FCSTD DOCUMENT  (FreeCAD 0.19R)
Label: Printer_assembly
License: All rights reserved
LicenseURL: http://en.wikipedia.org/wiki/All_rights_reserved
objects: App::Link×12, App::DocumentObjectGroup×4, Part::FeaturePython×2, App::AnnotationLabel×2, PartDesign::CoordinateSystem×1, App::FeaturePython×1, App::Part×1
note: 3 computed .brp shape members not serialized (recipe doc carries the construction recipe); baked Part::Feature solids carry a one-line shape summary decoded from their .brp
EXTERNAL_REF file=bed_aluminum.FCStd obj=Local_CS
EXTERNAL_REF file=bed_aluminum.FCStd obj=Body
EXTERNAL_REF file=extruder_head_gear.FCStd obj=Local_CS001
EXTERNAL_REF file=extruder_head_gear.FCStd obj=Body
EXTERNAL_REF file=angle_machined_2in_25.FCStd obj=Local_CS004
EXTERNAL_REF file=extruder_head_gear.FCStd obj=Local_CS
EXTERNAL_REF file=angle_machined_2in_25.FCStd obj=Body
EXTERNAL_REF file=angle_machined_2in_25.FCStd obj=Local_CS
EXTERNAL_REF file=motor stepper extruder.FCStd obj=Local_CS001
EXTERNAL_REF file=motor stepper extruder.FCStd obj=Body
EXTERNAL_REF file=angle_machined_2in_25.FCStd obj=Local_CS001
EXTERNAL_REF file=bearing_linear_8mm.FCStd obj=Local_CS
EXTERNAL_REF file=bearing_linear_8mm.FCStd obj=Body
EXTERNAL_REF file=angle_machined_2in_25.FCStd obj=Local_CS002
EXTERNAL_REF file=bearing_linear_8mm.FCStd obj=Local_CS001
EXTERNAL_REF file=screw_shc_M3x12.FCStd obj=Local_CS
EXTERNAL_REF file=screw_shc_M3x12.FCStd obj=Body
EXTERNAL_REF file=angle_machined_2in_25.FCStd obj=Local_CS005
EXTERNAL_REF file=washer_M5.FCStd obj=Local_CS
EXTERNAL_REF file=washer_M5.FCStd obj=Body
EXTERNAL_REF file=screw_shc_M3x16.FCStd obj=Local_CS
EXTERNAL_REF file=screw_shc_M3x16.FCStd obj=Body
EXTERNAL_REF file=Hex_Nut_M3.FCstd obj=Local_CS
EXTERNAL_REF file=washer_M5.FCStd obj=Local_CS001
EXTERNAL_REF file=Hex_Nut_M3.FCstd obj=Body
EXTERNAL_REF file=angle_machined_2in_25.FCStd obj=Local_CS006
EXTERNAL_REF file=nut_lead_screw_tr8x4.FCStd obj=Local_CS001
EXTERNAL_REF file=nut_lead_screw_tr8x4.FCStd obj=Body
EXTERNAL_REF file=drive_side_x-axis.FCStd obj=LCS_Origin
EXTERNAL_REF file=drive_side_x-axis.FCStd obj=Assembly

FEATURE [App::DocumentObjectGroup] Parts
FEATURE [PartDesign::CoordinateSystem] LCS_Origin
  AttacherType = Attacher::AttachEngine3D
  MapMode = 2
  Support = -> [X_Axis]
FEATURE [App::FeaturePython] Variables  # WARN: FeaturePython — macro-defined, semantics opaque (R4)
  Type = App::PropertyContainer
FEATURE [App::DocumentObjectGroup] Constraints
FEATURE [App::DocumentObjectGroup] Configurations
FEATURE [App::Link] bed
  AttachedBy = #Local_CS
  AttachedTo = Parent Assembly#LCS_Origin
  LinkPlacement = pos=(0,0,-6.35) rot=(0,0,1;0rad)
  LinkedObject = -> <external bed_aluminum.FCStd>#Body
  Placement = pos=(0,0,-6.35) rot=(0,0,1;0rad)
  SolverId = Placement::ExpressionEngine
  expr: Placement = LCS_Origin.Placement * AttachmentOffset * bed_aluminum#Local_CS.Placement ^ -1
FEATURE [App::Link] Body  label="Extruder"
  AttachedBy = #Local_CS001
  AttachedTo = bed#Local_CS
  AttachmentOffset = pos=(0,0,310) rot=(0,0,1;0rad)
  LinkPlacement = pos=(-15,-0.9652,380) rot=(0,0,1;0rad)
  LinkedObject = -> <external extruder_head_gear.FCStd>#Body
  Placement = pos=(-15,-0.9652,380) rot=(0,0,1;0rad)
  SolverId = Placement::ExpressionEngine
  expr: Placement = bed.Placement * bed_aluminum#Local_CS.Placement * AttachmentOffset * extruder_head_gear#Local_CS001.Placement ^ -1
FEATURE [App::Link] Bracket_extruder
  AttachedBy = #Local_CS004
  AttachedTo = Body#Local_CS
  AttachmentOffset = pos=(0,0,0) rot=(0,1,0;3.14159rad)
  LinkPlacement = pos=(-43,13.716,380) rot=(-1,0,0;3.14159rad)
  LinkedObject = -> <external angle_machined_2in_25.FCStd>#Body
  Placement = pos=(-43,13.716,380) rot=(-1,0,0;3.14159rad)
  SolverId = Placement::ExpressionEngine
  expr: Placement = Body.Placement * extruder_head_gear#Local_CS.Placement * AttachmentOffset * angle_machined_2in_25#Local_CS004.Placement ^ -1
FEATURE [App::Link] Body001  label="Motor_extruder"
  AttachedBy = #Local_CS001
  AttachedTo = Bracket_extruder#Local_CS
  AttachmentOffset = pos=(0,0,0) rot=(0,0,1;1.5708rad)
  LinkPlacement = pos=(-15,42.4785,380) rot=(-0.57735,-0.57735,0.57735;4.18879rad)
  LinkedObject = -> <external motor stepper extruder.FCStd>#Body
  Placement = pos=(-15,42.4785,380) rot=(-0.57735,-0.57735,0.57735;4.18879rad)
  SolverId = Placement::ExpressionEngine
  expr: Placement = Bracket_extruder.Placement * angle_machined_2in_25#Local_CS.Placement * AttachmentOffset * motor_stepper_extruder#Local_CS001.Placement ^ -1
FEATURE [App::Link] bearing_linear_8mm
  AttachedBy = #Local_CS
  AttachedTo = Bracket_extruder#Local_CS001
  AttachmentOffset = pos=(0,0,0) rot=(0,1,0;3.14159rad)
  LinkPlacement = pos=(-48,27.716,420) rot=(0.57735,-0.57735,0.57735;4.18879rad)
  LinkedObject = -> <external bearing_linear_8mm.FCStd>#Body
  Placement = pos=(-48,27.716,420) rot=(0.57735,-0.57735,0.57735;4.18879rad)
  SolverId = Placement::ExpressionEngine
  expr: Placement = Bracket_extruder.Placement * angle_machined_2in_25#Local_CS001.Placement * AttachmentOffset * bearing_linear_8mm#Local_CS.Placement ^ -1
FEATURE [App::Link] Body002  label="bearing_linear_8mm_2"
  AttachedBy = #Local_CS
  AttachedTo = Bracket_extruder#Local_CS002
  AttachmentOffset = pos=(0,0,0) rot=(0,1,0;3.14159rad)
  LinkPlacement = pos=(-48,27.716,340) rot=(0.57735,-0.57735,0.57735;4.18879rad)
  LinkedObject = -> <external bearing_linear_8mm.FCStd>#Body
  Placement = pos=(-48,27.716,340) rot=(0.57735,-0.57735,0.57735;4.18879rad)
  SolverId = Placement::ExpressionEngine
  expr: Placement = Bracket_extruder.Placement * angle_machined_2in_25#Local_CS002.Placement * AttachmentOffset * bearing_linear_8mm#Local_CS.Placement ^ -1
FEATURE [App::Link] screw_shc_M3x12
  AttachedBy = #Local_CS
  AttachedTo = bearing_linear_8mm#Local_CS001
  LinkPlacement = pos=(-32.9,27.716,432) rot=(0.57735,0.57735,0.57735;2.0944rad)
  LinkedObject = -> <external screw_shc_M3x12.FCStd>#Body
  Placement = pos=(-32.9,27.716,432) rot=(0.57735,0.57735,0.57735;2.0944rad)
  SolverId = Placement::ExpressionEngine
  expr: Placement = bearing_linear_8mm.Placement * bearing_linear_8mm#Local_CS001.Placement * AttachmentOffset * screw_shc_M3x12#Local_CS.Placement ^ -1
FEATURE [App::Link] washer_M5
  AttachedBy = #Local_CS
  AttachedTo = Bracket_extruder#Local_CS005
  LinkPlacement = pos=(-36.4,27.716,432) rot=(0,0,-1;1.5708rad)
  LinkedObject = -> <external washer_M5.FCStd>#Body
  Placement = pos=(-36.4,27.716,432) rot=(0,0,-1;1.5708rad)
  SolverId = Placement::ExpressionEngine
  expr: Placement = Bracket_extruder.Placement * angle_machined_2in_25#Local_CS005.Placement * AttachmentOffset * washer_M5#Local_CS.Placement ^ -1
FEATURE [App::Link] screw_shc_m3x16
  AttachedBy = #Local_CS
  AttachedTo = bearing_linear_8mm#Local_CS001
  LinkPlacement = pos=(-28.9,27.716,432) rot=(0.57735,0.57735,0.57735;2.0944rad)
  LinkedObject = -> <external screw_shc_M3x16.FCStd>#Body
  Placement = pos=(-28.9,27.716,432) rot=(0.57735,0.57735,0.57735;2.0944rad)
  SolverId = Placement::ExpressionEngine
  expr: Placement = bearing_linear_8mm.Placement * bearing_linear_8mm#Local_CS001.Placement * AttachmentOffset * screw_shc_M3x16#Local_CS.Placement ^ -1
FEATURE [App::Link] Body003  label="M3_nut"
  AttachedBy = #Local_CS
  AttachedTo = washer_M5#Local_CS001
  AttachmentOffset = pos=(0,0,0) rot=(0,1,0;3.14159rad)
  LinkPlacement = pos=(-34.95,27.716,432) rot=(0.250563,-0.935113,-0.250563;1.63783rad)
  LinkedObject = -> <external Hex_Nut_M3.FCstd>#Body
  Placement = pos=(-34.95,27.716,432) rot=(0.250563,-0.935113,-0.250563;1.63783rad)
  SolverId = Placement::ExpressionEngine
  expr: Placement = washer_M5.Placement * washer_M5#Local_CS001.Placement * AttachmentOffset * Hex_Nut_M3#Local_CS.Placement ^ -1
FEATURE [App::Link] nut_lead_screw_y
  AttachedBy = #Local_CS001
  AttachedTo = Bracket_extruder#Local_CS006
  LinkPlacement = pos=(-47,52.716,380) rot=(-0.678598,0.281085,0.678598;3.68962rad)
  LinkedObject = -> <external nut_lead_screw_tr8x4.FCStd>#Body
  Placement = pos=(-47,52.716,380) rot=(-0.678598,0.281085,0.678598;3.68962rad)
  SolverId = Placement::ExpressionEngine
  expr: Placement = Bracket_extruder.Placement * angle_machined_2in_25#Local_CS006.Placement * AttachmentOffset * nut_lead_screw_tr8x4#Local_CS001.Placement ^ -1
FEATURE [App::Link] drive_side_x_axis
  AttachedBy = #LCS_Origin
  AttachedTo = nut_lead_screw_y#Local_CS001
  AttachmentOffset = pos=(0,0,249.35) rot=(0,1,0;3.14159rad)
  LinkPlacement = pos=(206.35,52.716,380) rot=(0,1,0;4.71239rad)
  LinkedObject = -> <external drive_side_x-axis.FCStd>#Assembly
  Placement = pos=(206.35,52.716,380) rot=(0,1,0;4.71239rad)
  SolverId = Placement::ExpressionEngine
  expr: Placement = nut_lead_screw_y.Placement * nut_lead_screw_tr8x4#Local_CS001.Placement * AttachmentOffset * drive_side_x_axis#LCS_Origin.Placement ^ -1
FEATURE [App::Part] Assembly
  AssemblyType = Part::Link
  Group = -> [LCS_Origin,Variables,Constraints,Configurations,bed,Body,Bracket_extruder,Body001,bearing_linear_8mm,Body002,screw_shc_M3x12,washer_M5,screw_shc_m3x16,Body003,nut_lead_screw_y,drive_side_x_axis]
  Origin = -> Origin
  Type = Assembly
FEATURE [Part::FeaturePython] DistPoints  # WARN: FeaturePython — macro-defined, semantics opaque (R4)
FEATURE [App::AnnotationLabel] MeasureLbl
  BasePosition = (-206.5,13.716,320)
  LabelText = D = 13.0000 mm
  TextPosition = (0,0,0)
FEATURE [Part::FeaturePython] DistPoints001  # WARN: FeaturePython — macro-defined, semantics opaque (R4)
FEATURE [App::AnnotationLabel] MeasureLbl001
  BasePosition = (225.4,19.916,411)
  LabelText = D  = 81.1073 mm | ΔX = -50.799 | ΔY = 12.400 | ΔZ = 62.000
  TextPosition = (0,0,0)
FEATURE [App::DocumentObjectGroup] Measures
  Group = -> [DistPoints,MeasureLbl,DistPoints001,MeasureLbl001]

RESOLVED EXTERNAL PARTS (link-assembly join: the EXTERNAL_REF files above that resolve inside this repo's crawl, each included once):
---- part Hex_Nut_M3.FCstd = doc fcstd_daaefb471c37 ----
FCSTD DOCUMENT  (FreeCAD 0.19R)
Label: Hex_Nut_M3
License: All rights reserved
LicenseURL: http://en.wikipedia.org/wiki/All_rights_reserved
objects: PartDesign::CoordinateSystem×2, Part::Feature×1, PartDesign::FeatureBase×1, PartDesign::Body×1
note: 5 computed .brp shape members not serialized (recipe doc carries the construction recipe); baked Part::Feature solids carry a one-line shape summary decoded from their .brp

FEATURE [Part::Feature] _1828A211_18_8_Stainless_Steel_Hex_Nut
  shape: bbox 6.351 x 6.351 x 2.771 mm, 48 faces, 0 solids (baked)
FEATURE [PartDesign::FeatureBase] BaseFeature
  BaseFeature = -> _1828A211_18_8_Stainless_Steel_Hex_Nut
FEATURE [PartDesign::CoordinateSystem] Local_CS
  AttacherType = Attacher::AttachEngine3D
  MapMode = 11
  Placement = pos=(-4e-16,4e-16,1.2) rot=(-0.258819,0.965926,0;3.14159rad)
  Support = -> [BaseFeature]
FEATURE [PartDesign::CoordinateSystem] Local_CS001
  AttacherType = Attacher::AttachEngine3D
  AttachmentOffset = pos=(0,0,0) rot=(0,0,1;1.5708rad)
  MapMode = 11
  Placement = pos=(7e-16,-4e-16,-1.2) rot=(0,0,1;2.0944rad)
  Support = -> [BaseFeature]
FEATURE [PartDesign::Body] Body
  BaseFeature = -> _1828A211_18_8_Stainless_Steel_Hex_Nut
  Group = -> [BaseFeature,Local_CS,Local_CS001]
  Origin = -> Origin
  Tip = -> BaseFeature
---- part angle_machined_2in_25.FCStd = doc fcstd_c500b0d28d3c ----
FCSTD DOCUMENT  (FreeCAD 0.19R)
Label: angle_machined_2in_25
License: All rights reserved
LicenseURL: http://en.wikipedia.org/wiki/All_rights_reserved
objects: Sketcher::SketchObject×7, PartDesign::CoordinateSystem×7, PartDesign::Pocket×6, PartDesign::Pad×2, PartDesign::Mirrored×2, PartDesign::Fillet×1, PartDesign::LinearPattern×1, PartDesign::Body×1
note: 36 computed .brp shape members not serialized (recipe doc carries the construction recipe); baked Part::Feature solids carry a one-line shape summary decoded from their .brp

FEATURE [Sketcher::SketchObject] Sketch
  FullyConstrained = true
  MapMode = 5
  Support = -> [XY_Plane]
  sketch-geometry (6):
    g0: LineSegment StartX=0 StartY=0 StartZ=0 EndX=50.8 EndY=0 EndZ=0
    g1: LineSegment StartX=50.8 StartY=0 StartZ=0 EndX=50.8 EndY=-6.35 EndZ=0
    g2: LineSegment StartX=50.8 StartY=-6.35 StartZ=0 EndX=6.35 EndY=-6.35 EndZ=0
    g3: LineSegment StartX=6.35 StartY=-6.35 StartZ=0 EndX=6.35 EndY=-50.8 EndZ=0
    g4: LineSegment StartX=6.35 StartY=-50.8 StartZ=0 EndX=0 EndY=-50.8 EndZ=0
    g5: LineSegment StartX=0 StartY=-50.8 StartZ=0 EndX=0 EndY=0 EndZ=0
  constraints (17):
    c: Coincident(g-1,g0)
    c: PointOnObject(g0,g-1)
    c: Coincident(g0,g1)
    c: Vertical(g1)
    c: Coincident(g1,g2)
    c: Horizontal(g2)
    c: Coincident(g2,g3)
    c: Vertical(g3)
    c: Coincident(g3,g4)
    c: PointOnObject(g4,g-2)
    c: Horizontal(g4)
    c: Coincident(g4,g5)
    c: Coincident(g5,g0)
    c: Equal(g1,g4)
    c: DistanceY(g1,g1) = 6.35
    c: DistanceX(g0,g0) = 50.8
    c: Equal(g0,g5)
FEATURE [PartDesign::Pad] Pad
  Direction = (1,1,1)
  Length = 56
  Length2 = 100
  Profile = -> Sketch
  Refine = true
  Reversed = true
  Type = 0
FEATURE [Sketcher::SketchObject] Sketch001
  FullyConstrained = true
  MapMode = 5
  Placement = pos=(0,0,0) rot=(0.57735,0.57735,0.57735;2.0944rad)
  Support = -> [YZ_Plane]
  sketch-geometry (3):
    g0: Circle CenterX=-14 CenterY=-40 CenterZ=0 NormalX=0 NormalY=0 NormalZ=1 AngleXU=0 Radius=7.9375
    g1: Circle CenterX=-14 CenterY=-28 CenterZ=0 NormalX=0 NormalY=0 NormalZ=1 AngleXU=0 Radius=2
    g2: Circle CenterX=-14 CenterY=-52 CenterZ=0 NormalX=0 NormalY=0 NormalZ=1 AngleXU=0 Radius=2
  constraints (8):
    c: Diameter(g0) = 15.875
    c: Diameter(g1) = 4
    c: Equal(g1,g2)
    c: Symmetric(g1,g2,g0)
    c: Vertical(g1,g0)
    c: Distance(g1,g2) = 24
    c: DistanceX(g0,g-1) = 14
    c: DistanceY(g0,g-1) = 40
FEATURE [Sketcher::SketchObject] Sketch002
  FullyConstrained = true
  MapMode = 5
  Placement = pos=(0,0,0) rot=(0.57735,0.57735,0.57735;2.0944rad)
  Support = -> [YZ_Plane]
  sketch-geometry (8):
    g0: Circle CenterX=-39 CenterY=0 CenterZ=0 NormalX=0 NormalY=0 NormalZ=1 AngleXU=0 Radius=5.35781
    g1: Circle CenterX=-39 CenterY=0 CenterZ=0 NormalX=0 NormalY=0 NormalZ=1 AngleXU=0 Radius=8
    g2: Circle CenterX=-44.6569 CenterY=5.65685 CenterZ=0 NormalX=0 NormalY=0 NormalZ=1 AngleXU=0 Radius=1.5875
    g3: Circle CenterX=-33.3431 CenterY=5.65685 CenterZ=0 NormalX=0 NormalY=0 NormalZ=1 AngleXU=0 Radius=1.5875
    g4: Circle CenterX=-33.3431 CenterY=-5.65685 CenterZ=0 NormalX=0 NormalY=0 NormalZ=1 AngleXU=0 Radius=1.5875
    g5: Circle CenterX=-44.6569 CenterY=-5.65685 CenterZ=0 NormalX=0 NormalY=0 NormalZ=1 AngleXU=0 Radius=1.5875
    g6: LineSegment StartX=-44.6569 StartY=5.65685 StartZ=0 EndX=-33.3431 EndY=5.65685 EndZ=0
    g7: LineSegment StartX=-33.3431 StartY=5.65685 StartZ=0 EndX=-33.3431 EndY=-5.65685 EndZ=0
  constraints (19):
    c: Diameter(g0) = 10.7156
    c: Horizontal(g0,g-1)
    c: Coincident(g1,g0)
    c: Diameter(g1) = 16
    c: PointOnObject(g2,g1)
    c: PointOnObject(g3,g1)
    c: Equal(g2,g3)
    c: Equal(g3,g4)
    c: Equal(g4,g5)
    c: Symmetric(g2,g4,g0)
    c: Symmetric(g3,g5,g0)
    c: Horizontal(g3,g2)
    c: DistanceX(g0,g-1) = 39
    c: Coincident(g6,g2)
    c: Coincident(g6,g3)
    c: Coincident(g7,g3)
    c: Coincident(g7,g4)
    c: Equal(g6,g7)
    c: Diameter(g3) = 3.175
FEATURE [Sketcher::SketchObject] Sketch003
  FullyConstrained = true
  MapMode = 5
  Placement = pos=(0,0,0) rot=(1,0,0;1.5708rad)
  Support = -> [XZ_Plane]
  sketch-geometry (4):
    g0: LineSegment StartX=6.35 StartY=76.1187 StartZ=0 EndX=66.35 EndY=76.1187 EndZ=0
    g1: LineSegment StartX=66.35 StartY=76.1187 StartZ=0 EndX=66.35 EndY=25 EndZ=0
    g2: LineSegment StartX=66.35 StartY=25 StartZ=0 EndX=6.35 EndY=25 EndZ=0
    g3: LineSegment StartX=6.35 StartY=25 StartZ=0 EndX=6.35 EndY=76.1187 EndZ=0
  constraints (12):
    c: Coincident(g0,g1)
    c: Coincident(g1,g2)
    c: Coincident(g2,g3)
    c: Coincident(g3,g0)
    c: Horizontal(g0)
    c: Horizontal(g2)
    c: Vertical(g1)
    c: Vertical(g3)
    c: DistanceY(g3,g3) = 51.1187
    c: DistanceY(g-1,g2) = 25
    c: DistanceX(g0,g0) = 60
    c: DistanceX(g-1,g0) = 6.35
FEATURE [Sketcher::SketchObject] Sketch004
  FullyConstrained = true
  MapMode = 5
  Placement = pos=(0,0,0) rot=(1,0,0;1.5708rad)
  Support = -> [XZ_Plane]
  sketch-geometry (7):
    g0: Circle CenterX=43.5 CenterY=15.5 CenterZ=0 NormalX=0 NormalY=0 NormalZ=1 AngleXU=0 Radius=1.865
    g1: Circle CenterX=43.5 CenterY=-15.5 CenterZ=0 NormalX=0 NormalY=0 NormalZ=1 AngleXU=0 Radius=1.865
    g2: Circle CenterX=12.5 CenterY=15.5 CenterZ=0 NormalX=0 NormalY=0 NormalZ=1 AngleXU=0 Radius=1.865
    g3: Circle CenterX=12.5 CenterY=-15.5 CenterZ=0 NormalX=0 NormalY=0 NormalZ=1 AngleXU=0 Radius=1.865
    g4: LineSegment StartX=0 StartY=0 StartZ=0 EndX=-20.31 EndY=0 EndZ=0
    g5: LineSegment StartX=28 StartY=0 StartZ=0 EndX=28 EndY=70 EndZ=0
    g6: Circle CenterX=28 CenterY=0 CenterZ=0 NormalX=0 NormalY=0 NormalZ=1 AngleXU=0 Radius=11.1125
  constraints (18):
    c: Horizontal(g4)
    c: Coincident(g4,g-1)
    c: Distance(g4) = 20.31
    c: Vertical(g5)
    c: Horizontal(g5,g-1)
    c: Symmetric(g2,g0,g5)
    c: Symmetric(g2,g3,g4)
    c: Symmetric(g0,g1,g4)
    c: DistanceX(g2,g0) = 31
    c: Equal(g2,g0)
    c: Equal(g1,g0)
    c: Equal(g1,g3)
    c: Diameter(g0) = 3.73
    c: DistanceY(g1,g0) = 31
    c: DistanceX(g-1,g5) = 28  'motor_x'
    c: DistanceY(g5,g5) = 70
    c: Coincident(g6,g5)
    c: Diameter(g6) = 22.225
FEATURE [PartDesign::Pad] Pad001
  BaseFeature = -> Pad
  Direction = (1,1,1)
  Length = 56
  Length2 = 100
  Profile = -> Sketch
  Refine = true
  Type = 0
FEATURE [PartDesign::Fillet] Fillet
  Base = -> Pad001 [Edge17,Edge18,Edge16]
  BaseFeature = -> Pad001
  Radius = 4.5
  Refine = true
  SupportTransform = false
FEATURE [PartDesign::Pocket] Pocket  label="top_bearing"
  BaseFeature = -> Fillet
  Length = 20
  Length2 = 100
  Profile = -> Sketch001
  Refine = true
  Reversed = true
  Type = 1
FEATURE [PartDesign::LinearPattern] LinearPattern  label="LinearPattern_lower_bearing"
  BaseFeature = -> Pocket
  Direction = -> Sketch001 [V_Axis]
  Length = 80
  Occurrences = 2
  Originals = -> [Pocket]
  Refine = true
FEATURE [PartDesign::Pocket] Pocket001  label="nut_pocket"
  BaseFeature = -> LinearPattern
  Length = 5
  Length2 = 100
  Midplane = true
  Profile = -> Sketch002
  Refine = true
  Reversed = true
  Type = 1
FEATURE [PartDesign::Pocket] Pocket002
  BaseFeature = -> Pocket001
  Length = 5
  Length2 = 100
  Midplane = true
  Profile = -> Sketch003
  Refine = true
  Type = 1
FEATURE [PartDesign::Mirrored] Mirrored001
  BaseFeature = -> Pocket002
  MirrorPlane = -> Sketch003 [H_Axis]
  Originals = -> [Pocket002]
  Refine = true
FEATURE [PartDesign::Pocket] Pocket003
  BaseFeature = -> Mirrored001
  Length = 5
  Length2 = 100
  Midplane = true
  Profile = -> Sketch004
  Type = 1
FEATURE [Sketcher::SketchObject] Sketch005
  FullyConstrained = true
  MapMode = 5
  Support = -> [XY_Plane]
  sketch-geometry (4):
    g0: LineSegment StartX=6.35 StartY=-4.7625 StartZ=0 EndX=66.35 EndY=-4.7625 EndZ=0
    g1: LineSegment StartX=66.35 StartY=-4.7625 StartZ=0 EndX=66.35 EndY=-17.0125 EndZ=0
    g2: LineSegment StartX=66.35 StartY=-17.0125 StartZ=0 EndX=6.35 EndY=-17.0125 EndZ=0
    g3: LineSegment StartX=6.35 StartY=-17.0125 StartZ=0 EndX=6.35 EndY=-4.7625 EndZ=0
  constraints (12):
    c: Coincident(g0,g1)
    c: Coincident(g1,g2)
    c: Coincident(g2,g3)
    c: Coincident(g3,g0)
    c: Horizontal(g0)
    c: Horizontal(g2)
    c: Vertical(g1)
    c: Vertical(g3)
    c: DistanceY(g1,g1) = 12.25
    c: DistanceX(g0,g0) = 60
    c: DistanceX(g-1,g0) = 6.35
    c: DistanceY(g0,g-1) = 4.7625
FEATURE [PartDesign::Pocket] Pocket004
  BaseFeature = -> Pocket003
  Length = 5
  Length2 = 100
  Midplane = true
  Profile = -> Sketch005
  Refine = true
  Type = 1
FEATURE [PartDesign::CoordinateSystem] Local_CS001  label="bearing_top"
  AttacherType = Attacher::AttachEngine3D
  MapMode = 11
  Placement = pos=(0,-14,-40) rot=(0.707107,0,0.707107;3.14159rad)
  Support = -> [Pocket004]
FEATURE [PartDesign::CoordinateSystem] Local_CS002  label="bearing_bottom"
  AttacherType = Attacher::AttachEngine3D
  MapMode = 11
  Placement = pos=(-1.8e-14,-14,40) rot=(0.707107,0,0.707107;3.14159rad)
  Support = -> [Pocket004]
FEATURE [PartDesign::CoordinateSystem] Local_CS003  label="nut"
  AttacherType = Attacher::AttachEngine3D
  AttachmentOffset = pos=(0,0,0) rot=(0,1,0;3.14159rad)
  MapMode = 11
  Placement = pos=(0,-44.6569,5.65685) rot=(-0.707107,0,0.707107;3.14159rad)
  Support = -> [Pocket004]
FEATURE [PartDesign::CoordinateSystem] Local_CS004  label="extruder"
  AttacherType = Attacher::AttachEngine3D
  MapMode = 11
  Placement = pos=(28,0,0) rot=(0.57735,-0.57735,0.57735;2.0944rad)
  Support = -> [Pocket004]
FEATURE [PartDesign::CoordinateSystem] Local_CS006  label="lcs_nut"
  AttacherType = Attacher::AttachEngine3D
  MapMode = 11
  Placement = pos=(0,-39,1.61e-14) rot=(0.707107,0,0.707107;3.14159rad)
  Support = -> [Pocket004]
FEATURE [Sketcher::SketchObject] Sketch006
  FullyConstrained = true
  MapMode = 5
  Placement = pos=(0,0,0) rot=(0.57735,0.57735,0.57735;2.0944rad)
  Support = -> [YZ_Plane]
  sketch-geometry (4):
    g0: LineSegment StartX=-62.1666 StartY=69.7638 StartZ=0 EndX=-24.8 EndY=69.7638 EndZ=0
    g1: LineSegment StartX=-24.8 StartY=69.7638 StartZ=0 EndX=-24.8 EndY=25 EndZ=0
    g2: LineSegment StartX=-24.8 StartY=25 StartZ=0 EndX=-62.1666 EndY=25 EndZ=0
    g3: LineSegment StartX=-62.1666 StartY=25 StartZ=0 EndX=-62.1666 EndY=69.7638 EndZ=0
  constraints (12):
    c: Coincident(g0,g1)
    c: Coincident(g1,g2)
    c: Coincident(g2,g3)
    c: Coincident(g3,g0)
    c: Horizontal(g0)
    c: Horizontal(g2)
    c: Vertical(g1)
    c: Vertical(g3)
    c: DistanceX(g0,g-1) = 24.8
    c: DistanceY(g-1,g1) = 25
    c: DistanceX(g2,g2) = 37.3666
    c: DistanceY(g3,g3) = 44.7638
FEATURE [PartDesign::Pocket] Pocket005
  BaseFeature = -> Pocket004
  Length = 5
  Length2 = 100
  Midplane = true
  Profile = -> Sketch006
  Refine = true
  Type = 1
FEATURE [PartDesign::Mirrored] Mirrored
  BaseFeature = -> Pocket005
  MirrorPlane = -> Sketch006 [H_Axis]
  Originals = -> [Pocket005]
  Refine = true
FEATURE [PartDesign::CoordinateSystem] Local_CS  label="motor_extruder"
  AttacherType = Attacher::AttachEngine3D
  MapMode = 11
  Placement = pos=(28,-4.7625,-1.1e-15) rot=(0.57735,-0.57735,0.57735;2.0944rad)
  Support = -> [Mirrored]
FEATURE [PartDesign::CoordinateSystem] Local_CS005  label="lcs_top_screw"
  AttacherType = Attacher::AttachEngine3D
  MapMode = 11
  Placement = pos=(6.35,-14,-52) rot=(0.707107,0,-0.707107;3.14159rad)
  Support = -> [Mirrored]
FEATURE [PartDesign::Body] Body
  Group = -> [Sketch,Pad,Pad001,Sketch001,Fillet,Pocket,Sketch002,LinearPattern,Pocket001,Sketch003,Pocket002,Mirrored001,Sketch004,Pocket003,Local_CS001,Local_CS002,Local_CS003,Sketch005,Pocket004,Local_CS,Local_CS004,Local_CS005,Local_CS006,Sketch006,Pocket005,Mirrored]
  Origin = -> Origin
  Tip = -> Mirrored
---- part bearing_linear_8mm.FCStd = doc fcstd_97f1be51743a ----
FCSTD DOCUMENT  (FreeCAD 0.19R)
Label: bearing_linear_8mm
License: All rights reserved
LicenseURL: http://en.wikipedia.org/wiki/All_rights_reserved
objects: Sketcher::SketchObject×3, PartDesign::CoordinateSystem×3, PartDesign::Revolution×1, PartDesign::Pocket×1, PartDesign::Mirrored×1, PartDesign::Hole×1, PartDesign::Body×1
note: 14 computed .brp shape members not serialized (recipe doc carries the construction recipe); baked Part::Feature solids carry a one-line shape summary decoded from their .brp

FEATURE [Sketcher::SketchObject] Sketch
  FullyConstrained = true
  MapMode = 5
  Placement = pos=(0,0,0) rot=(1,0,0;1.5708rad)
  Support = -> [XZ_Plane]
  sketch-geometry (6):
    g0: LineSegment StartX=16 StartY=0 StartZ=0 EndX=16 EndY=5 EndZ=0
    g1: LineSegment StartX=16 StartY=5 StartZ=0 EndX=7.5 EndY=5 EndZ=0
    g2: LineSegment StartX=7.5 StartY=5 StartZ=0 EndX=7.5 EndY=24 EndZ=0
    g3: LineSegment StartX=7.5 StartY=24 StartZ=0 EndX=4 EndY=24 EndZ=0
    g4: LineSegment StartX=4 StartY=24 StartZ=0 EndX=4 EndY=0 EndZ=0
    g5: LineSegment StartX=4 StartY=0 StartZ=0 EndX=16 EndY=0 EndZ=0
  constraints (18):
    c: PointOnObject(g0,g-1)
    c: Vertical(g0)
    c: Coincident(g0,g1)
    c: Horizontal(g1)
    c: Coincident(g1,g2)
    c: Vertical(g2)
    c: Coincident(g2,g3)
    c: Horizontal(g3)
    c: Coincident(g3,g4)
    c: PointOnObject(g4,g-1)
    c: Vertical(g4)
    c: Coincident(g4,g5)
    c: Coincident(g5,g0)
    c: DistanceX(g-1,g4) = 4
    c: DistanceX(g-1,g2) = 7.5
    c: DistanceY(g-1,g2) = 24
    c: DistanceY(g0,g0) = 5
    c: DistanceX(g-1,g0) = 16
FEATURE [PartDesign::Revolution] Revolution
  Angle = 360
  Axis = (0,2e-16,1)
  Base = (0,0,0)
  Placement = pos=(0,0,0) rot=(1,0,0;1.5708rad)
  Profile = -> Sketch
  ReferenceAxis = -> Sketch [V_Axis]
  Reversed = true
FEATURE [Sketcher::SketchObject] Sketch001
  FullyConstrained = true
  MapMode = 5
  Support = -> [XY_Plane]
  sketch-geometry (5):
    g0: LineSegment StartX=10.5 StartY=20 StartZ=0 EndX=50.5 EndY=20 EndZ=0
    g1: LineSegment StartX=50.5 StartY=20 StartZ=0 EndX=50.5 EndY=-20 EndZ=0
    g2: LineSegment StartX=50.5 StartY=-20 StartZ=0 EndX=10.5 EndY=-20 EndZ=0
    g3: LineSegment StartX=10.5 StartY=20 StartZ=0 EndX=10.5 EndY=0 EndZ=0
    g4: LineSegment StartX=10.5 StartY=0 StartZ=0 EndX=10.5 EndY=-20 EndZ=0
  constraints (15):
    c: Coincident(g0,g1)
    c: Coincident(g1,g2)
    c: Horizontal(g0)
    c: Horizontal(g2)
    c: Vertical(g1)
    c: Coincident(g3,g0)
    c: Vertical(g3)
    c: Coincident(g4,g3)
    c: Coincident(g4,g2)
    c: Vertical(g4)
    c: Equal(g3,g4)
    c: Horizontal(g3,g-1)
    c: DistanceY(g1,g1) = 40
    c: DistanceX(g-1,g0) = 10.5
    c: Equal(g0,g1)
FEATURE [PartDesign::Pocket] Pocket
  BaseFeature = -> Revolution
  Length = 5
  Length2 = 100
  Midplane = true
  Placement = pos=(0,0,0) rot=(1,0,0;1.5708rad)
  Profile = -> Sketch001
  Type = 1
FEATURE [PartDesign::Mirrored] Mirrored
  BaseFeature = -> Pocket
  MirrorPlane = -> Sketch001 [V_Axis]
  Originals = -> [Pocket]
  Placement = pos=(0,0,0) rot=(1,0,0;1.5708rad)
FEATURE [Sketcher::SketchObject] Sketch002
  FullyConstrained = true
  MapMode = 5
  Support = -> [XY_Plane]
  sketch-geometry (2):
    g0: Circle CenterX=0 CenterY=12 CenterZ=0 NormalX=0 NormalY=0 NormalZ=1 AngleXU=0 Radius=1.75
    g1: Circle CenterX=0 CenterY=-12 CenterZ=0 NormalX=0 NormalY=0 NormalZ=1 AngleXU=0 Radius=1.75
  constraints (5):
    c: Equal(g0,g1)
    c: Diameter(g0) = 3.5
    c: Symmetric(g0,g1,g-1)
    c: Vertical(g-1,g0)
    c: DistanceY(g1,g0) = 24
FEATURE [PartDesign::Hole] Hole
  BaseFeature = -> Mirrored
  Depth = 25
  DepthType = 1
  Diameter = 3.4
  DrillForDepth = false
  DrillPoint = 1
  DrillPointAngle = 118
  HoleCutCountersinkAngle = 90
  HoleCutCustomValues = false
  HoleCutDepth = 3.1
  HoleCutDiameter = 6
  HoleCutType = 1
  ModelActualThread = false
  Placement = pos=(0,0,0) rot=(1,0,0;1.5708rad)
  Profile = -> Sketch002
  Refine = true
  Reversed = true
  Tapered = false
  TaperedAngle = 90
  ThreadAngle = 60
  ThreadClass = 0
  ThreadCutOffInner = 0.0270633
  ThreadCutOffOuter = 0.0541266
  ThreadDirection = 0
  ThreadFit = 0
  ThreadPitch = 0.25
  ThreadSize = 9
  ThreadType = 1
  Threaded = false
FEATURE [PartDesign::CoordinateSystem] Local_CS
  AttacherType = Attacher::AttachEngine3D
  MapMode = 11
  Placement = pos=(0,2.2e-15,5) rot=(0.707107,-0.707107,0;3.14159rad)
  Support = -> [Hole]
FEATURE [PartDesign::CoordinateSystem] Local_CS001  label="LCS_SCREW1"
  AttacherType = Attacher::AttachEngine3D
  MapMode = 11
  Placement = pos=(0,-12,3.1) rot=(0.707107,0.707107,0;3.14159rad)
  Support = -> [Hole]
FEATURE [PartDesign::CoordinateSystem] Local_CS002  label="LCS_SCREW2"
  AttacherType = Attacher::AttachEngine3D
  MapMode = 11
  Placement = pos=(0,12,3.1) rot=(0.707107,0.707107,0;3.14159rad)
  Support = -> [Hole]
FEATURE [PartDesign::Body] Body
  Group = -> [Sketch,Revolution,Sketch001,Pocket,Mirrored,Sketch002,Local_CS,Hole,Local_CS001,Local_CS002]
  Origin = -> Origin
  Tip = -> Hole
---- part bed_aluminum.FCStd = doc fcstd_8c2d4e9136e1 ----
FCSTD DOCUMENT  (FreeCAD 0.19R)
Label: bed_aluminum
License: All rights reserved
LicenseURL: http://en.wikipedia.org/wiki/All_rights_reserved
objects: Sketcher::SketchObject×2, PartDesign::Pad×1, PartDesign::CoordinateSystem×1, PartDesign::Hole×1, PartDesign::Body×1
note: 8 computed .brp shape members not serialized (recipe doc carries the construction recipe); baked Part::Feature solids carry a one-line shape summary decoded from their .brp

FEATURE [Sketcher::SketchObject] Sketch
  FullyConstrained = true
  MapMode = 5
  Support = -> [XY_Plane]
  sketch-geometry (4):
    g0: LineSegment StartX=-160 StartY=-160 StartZ=0 EndX=160 EndY=-160 EndZ=0
    g1: LineSegment StartX=160 StartY=-160 StartZ=0 EndX=160 EndY=160 EndZ=0
    g2: LineSegment StartX=160 StartY=160 StartZ=0 EndX=-160 EndY=160 EndZ=0
    g3: LineSegment StartX=-160 StartY=160 StartZ=0 EndX=-160 EndY=-160 EndZ=0
  constraints (11):
    c: Coincident(g0,g1)
    c: Coincident(g1,g2)
    c: Coincident(g2,g3)
    c: Coincident(g3,g0)
    c: Horizontal(g0)
    c: Horizontal(g2)
    c: Vertical(g1)
    c: Vertical(g3)
    c: Symmetric(g1,g0,g-1)
    c: DistanceY(g1,g1) = 320
    c: DistanceX(g0,g0) = 320
FEATURE [PartDesign::Pad] Pad
  Direction = (1,1,1)
  Length = 6.35
  Length2 = 100
  Profile = -> Sketch
  Refine = true
  Type = 0
FEATURE [PartDesign::CoordinateSystem] Local_CS
  AttacherType = Attacher::AttachEngine3D
  MapMode = 5
  Placement = pos=(0,0,6.35) rot=(0,0,1;0rad)
  Support = -> [Pad]
FEATURE [Sketcher::SketchObject] Sketch001
  FullyConstrained = true
  MapMode = 5
  Placement = pos=(0,0,6.35) rot=(0,0,1;0rad)
  Support = -> [Pad]
  expr: Constraints[10] = 310 - 70
  expr: Constraints[9] = 310 - 70
  sketch-geometry (8):
    g0: LineSegment StartX=-120 StartY=-120 StartZ=0 EndX=120 EndY=-120 EndZ=0
    g1: LineSegment StartX=120 StartY=-120 StartZ=0 EndX=120 EndY=120 EndZ=0
    g2: LineSegment StartX=120 StartY=120 StartZ=0 EndX=-120 EndY=120 EndZ=0
    g3: LineSegment StartX=-120 StartY=120 StartZ=0 EndX=-120 EndY=-120 EndZ=0
    g4: Circle CenterX=-120 CenterY=120 CenterZ=0 NormalX=0 NormalY=0 NormalZ=1 AngleXU=0 Radius=23.8807
    g5: Circle CenterX=120 CenterY=120 CenterZ=0 NormalX=0 NormalY=0 NormalZ=1 AngleXU=0 Radius=23.8807
    g6: Circle CenterX=120 CenterY=-120 CenterZ=0 NormalX=0 NormalY=0 NormalZ=1 AngleXU=0 Radius=23.8807
    g7: Circle CenterX=-120 CenterY=-120 CenterZ=0 NormalX=0 NormalY=0 NormalZ=1 AngleXU=0 Radius=23.8807
  constraints (19):
    c: Coincident(g0,g1)
    c: Coincident(g1,g2)
    c: Coincident(g2,g3)
    c: Coincident(g3,g0)
    c: Horizontal(g0)
    c: Horizontal(g2)
    c: Vertical(g1)
    c: Vertical(g3)
    c: Symmetric(g1,g0,g-1)
    c: DistanceY(g1,g1) = 240
    c: DistanceX(g0,g0) = 240
    c: Coincident(g4,g2)
    c: Coincident(g5,g1)
    c: Coincident(g6,g0)
    c: Coincident(g7,g0)
    c: Equal(g5,g4)
    c: Equal(g4,g7)
    c: Equal(g7,g6)
    c: Diameter(g5) = 47.7614
FEATURE [PartDesign::Hole] Hole
  BaseFeature = -> Pad
  Depth = 25
  DepthType = 1
  Diameter = 4.3
  DrillForDepth = false
  DrillPoint = 1
  DrillPointAngle = 118
  HoleCutCountersinkAngle = 90
  HoleCutCustomValues = false
  HoleCutDepth = 2.58
  HoleCutDiameter = 6.88
  HoleCutType = 2
  ModelActualThread = false
  Profile = -> Sketch001
  Refine = true
  Tapered = false
  TaperedAngle = 90
  ThreadAngle = 0
  ThreadClass = 0
  ThreadCutOffInner = 0
  ThreadCutOffOuter = 0
  ThreadDirection = 0
  ThreadFit = 1
  ThreadPitch = 0
  ThreadSize = 11
  ThreadType = 1
  Threaded = false
FEATURE [PartDesign::Body] Body
  Group = -> [Sketch,Pad,Local_CS,Sketch001,Hole]
  Origin = -> Origin
  Tip = -> Hole
---- part drive_side_x-axis.FCStd = doc fcstd_f4906b0e7a5b ----
FCSTD DOCUMENT  (FreeCAD 0.19R)
Label: drive_side_x-axis
License: All rights reserved
LicenseURL: http://en.wikipedia.org/wiki/All_rights_reserved
objects: App::Link×20, App::DocumentObjectGroup×3, PartDesign::CoordinateSystem×1, App::FeaturePython×1, App::Part×1
note: 1 computed .brp shape members not serialized (recipe doc carries the construction recipe); baked Part::Feature solids carry a one-line shape summary decoded from their .brp
EXTERNAL_REF file=angle_machined_2in_25_drive_side.FCStd obj=Local_CS010
EXTERNAL_REF file=bracket_nema_17.FCStd obj=Local_CS004
EXTERNAL_REF file=bracket_nema_17.FCStd obj=Body
EXTERNAL_REF file=bracket_nema_17.FCStd obj=Local_CS001
EXTERNAL_REF file=motor stepper 17hs4401s.FCStd obj=Local_CS
EXTERNAL_REF file=motor stepper 17hs4401s.FCStd obj=Body
EXTERNAL_REF file=coupling_8mm_5mm.FCStd obj=Local_CS
EXTERNAL_REF file=coupling_8mm_5mm.FCStd obj=Body
EXTERNAL_REF file=angle_machined_2in_25_drive_side.FCStd obj=Local_CS007
EXTERNAL_REF file=angle_machined_2in_25_drive_side.FCStd obj=Body
EXTERNAL_REF file=KFL08_bushing.FCStd obj=Local_CS001
EXTERNAL_REF file=KFL08_bushing.FCStd obj=Body
EXTERNAL_REF file=angle_machined_2in_25_drive_side.FCStd obj=Local_CS021
EXTERNAL_REF file=support_shaft_horiz_8mm.FCStd obj=Local_CS003
EXTERNAL_REF file=support_shaft_horiz_8mm.FCStd obj=Body
EXTERNAL_REF file=angle_machined_2in_25_drive_side.FCStd obj=Local_CS019
EXTERNAL_REF file=support_shaft_horiz_8mm.FCStd obj=Local_CS002
EXTERNAL_REF file=angle_machined_2in_25_drive_side.FCStd obj=Local_CS009
EXTERNAL_REF file=bearing_linear_8mm_horiz.FCStd obj=Local_CS
EXTERNAL_REF file=bearing_linear_8mm_horiz.FCStd obj=Body
EXTERNAL_REF file=angle_machined_2in_25_drive_side.FCStd obj=Local_CS
EXTERNAL_REF file=bearing_linear_8mm_horiz.FCStd obj=Local_CS004
EXTERNAL_REF file=shaft_8mm.FCStd obj=Local_CS
EXTERNAL_REF file=support_shaft_horiz_8mm.FCStd obj=Local_CS001
EXTERNAL_REF file=shaft_8mm.FCStd obj=Body
EXTERNAL_REF file=support_shaft_horiz_8mm.FCStd obj=Local_CS005
EXTERNAL_REF file=shaft_8mm.FCStd obj=Local_CS001
EXTERNAL_REF file=bearing_linear_8mm_horiz.FCStd obj=Local_CS003
EXTERNAL_REF file=bearing_linear_8mm_horiz.FCStd obj=Local_CS001
EXTERNAL_REF file=coupling_8mm_5mm.FCStd obj=Local_CS001
EXTERNAL_REF file=rod_threaded_8mm.FCStd obj=Local_CS001
EXTERNAL_REF file=rod_threaded_8mm.FCStd obj=Body
EXTERNAL_REF file=angle_machined_2in_25_drive_side.FCStd obj=Local_CS025
EXTERNAL_REF file=nut_angle.FCStd obj=Local_CS
EXTERNAL_REF file=nut_angle.FCStd obj=Body
EXTERNAL_REF file=nut_angle.FCStd obj=Local_CS001
EXTERNAL_REF file=nut_lead_screw_tr8x4.FCStd obj=Local_CS002
EXTERNAL_REF file=nut_lead_screw_tr8x4.FCStd obj=Body

FEATURE [App::DocumentObjectGroup] Parts
FEATURE [PartDesign::CoordinateSystem] LCS_Origin
  AttacherType = Attacher::AttachEngine3D
  MapMode = 2
  Support = -> [X_Axis]
FEATURE [App::FeaturePython] Variables  # WARN: FeaturePython — macro-defined, semantics opaque (R4)
  Type = App::PropertyContainer
FEATURE [App::DocumentObjectGroup] Constraints
FEATURE [App::DocumentObjectGroup] Configurations
FEATURE [App::Link] Body  label="bracket_nema_17"
  AttachedBy = #Local_CS004
  AttachedTo = Body003#Local_CS010
  AttachmentOffset = pos=(0,23,6.35) rot=(0,0,-1;4.71239rad)
  LinkPlacement = pos=(0.015,-4.15,-55.5) rot=(0,0,-1;3.14159rad)
  LinkedObject = -> <external bracket_nema_17.FCStd>#Body
  Placement = pos=(0.015,-4.15,-55.5) rot=(0,0,-1;3.14159rad)
  SolverId = Placement::ExpressionEngine
  expr: Placement = Body003.Placement * angle_machined_2in_25_drive_side#Local_CS010.Placement * AttachmentOffset * bracket_nema_17#Local_CS004.Placement ^ -1
FEATURE [App::Link] Body001  label="motor_nema"
  AttachedBy = #Local_CS
  AttachedTo = Body#Local_CS001
  AttachmentOffset = pos=(0,0,0) rot=(0.707107,0.707107,0;3.14159rad)
  LinkPlacement = pos=(0.015,0.35,-93.5) rot=(0,0,1;1.5708rad)
  LinkedObject = -> <external motor stepper 17hs4401s.FCStd>#Body
  Placement = pos=(0.015,0.35,-93.5) rot=(0,0,1;1.5708rad)
  SolverId = Placement::ExpressionEngine
  expr: Placement = Body.Placement * bracket_nema_17#Local_CS001.Placement * AttachmentOffset * motor_stepper_17hs4401s#Local_CS.Placement ^ -1
FEATURE [App::Link] Body002  label="coupling"
  AttachedBy = #Local_CS
  AttachedTo = Body001#Local_CS
  AttachmentOffset = pos=(0,0,-12) rot=(0,0,1;0rad)
  LinkPlacement = pos=(0.015,0.35,-31) rot=(0.707107,0.707107,0;3.14159rad)
  LinkedObject = -> <external coupling_8mm_5mm.FCStd>#Body
  Placement = pos=(0.015,0.35,-31) rot=(0.707107,0.707107,0;3.14159rad)
  SolverId = Placement::ExpressionEngine
  expr: Placement = Body001.Placement * motor_stepper_17hs4401s#Local_CS.Placement * AttachmentOffset * coupling_8mm_5mm#Local_CS.Placement ^ -1
FEATURE [App::Link] Body003  label="angle_machined_2in_25_drive"
  AttachedBy = #Local_CS007
  AttachedTo = Parent Assembly#LCS_Origin
  AttachmentOffset = pos=(0,0,0) rot=(0,1,0;3.14159rad)
  LinkPlacement = pos=(1.03e-14,-39,6.35) rot=(-0.707107,0,0.707107;3.14159rad)
  LinkedObject = -> <external angle_machined_2in_25_drive_side.FCStd>#Body
  Placement = pos=(1.03e-14,-39,6.35) rot=(-0.707107,0,0.707107;3.14159rad)
  SolverId = Placement::ExpressionEngine
  expr: Placement = LCS_Origin.Placement * AttachmentOffset * angle_machined_2in_25_drive_side#Local_CS007.Placement ^ -1
FEATURE [App::Link] Body004  label="bearing_axial1"
  AttachedBy = #Local_CS001
  AttachedTo = Body003#Local_CS007
  AttachmentOffset = pos=(0,0,0) rot=(0,0,1;3.14159rad)
  LinkPlacement = pos=(-3e-15,0,1.8e-15) rot=(0.707107,0.707107,0;3.14159rad)
  LinkedObject = -> <external KFL08_bushing.FCStd>#Body
  Placement = pos=(-3e-15,0,1.8e-15) rot=(0.707107,0.707107,0;3.14159rad)
  SolverId = Placement::ExpressionEngine
  expr: Placement = Body003.Placement * angle_machined_2in_25_drive_side#Local_CS007.Placement * AttachmentOffset * KFL08_bushing#Local_CS001.Placement ^ -1
FEATURE [App::Link] Body005  label="support_shaft_top"
  AttachedBy = #Local_CS003
  AttachedTo = Body003#Local_CS021
  AttachmentOffset = pos=(0,0,0) rot=(0.707107,0.707107,0;3.14159rad)
  LinkPlacement = pos=(40,-25,11.35) rot=(0,0,1;0rad)
  LinkedObject = -> <external support_shaft_horiz_8mm.FCStd>#Body
  Placement = pos=(40,-25,11.35) rot=(0,0,1;0rad)
  SolverId = Placement::ExpressionEngine
  expr: Placement = Body003.Placement * angle_machined_2in_25_drive_side#Local_CS021.Placement * AttachmentOffset * support_shaft_horiz_8mm#Local_CS003.Placement ^ -1
FEATURE [App::Link] Body006  label="support_shaft_other"
  AttachedBy = #Local_CS002
  AttachedTo = Body003#Local_CS019
  AttachmentOffset = pos=(0,0,0) rot=(0,0,1;1.5708rad)
  LinkPlacement = pos=(-40,-25,11.35) rot=(0,1,0;3.14159rad)
  LinkedObject = -> <external support_shaft_horiz_8mm.FCStd>#Body
  Placement = pos=(-40,-25,11.35) rot=(0,1,0;3.14159rad)
  SolverId = Placement::ExpressionEngine
  expr: Placement = Body003.Placement * angle_machined_2in_25_drive_side#Local_CS019.Placement * AttachmentOffset * support_shaft_horiz_8mm#Local_CS002.Placement ^ -1
FEATURE [App::Link] Body007  label="bearing_lin1"
  AttachedBy = #Local_CS
  AttachedTo = Body003#Local_CS009
  AttachmentOffset = pos=(0,0,0) rot=(0,1,0;3.14159rad)
  LinkPlacement = pos=(45,-50,-28.65) rot=(-0.57735,-0.57735,0.57735;4.18879rad)
  LinkedObject = -> <external bearing_linear_8mm_horiz.FCStd>#Body
  Placement = pos=(45,-50,-28.65) rot=(-0.57735,-0.57735,0.57735;4.18879rad)
  SolverId = Placement::ExpressionEngine
  expr: Placement = Body003.Placement * angle_machined_2in_25_drive_side#Local_CS009.Placement * AttachmentOffset * bearing_linear_8mm_horiz#Local_CS.Placement ^ -1
FEATURE [App::Link] bearing_lin2
  AttachedBy = #Local_CS004
  AttachedTo = Body003#Local_CS
  AttachmentOffset = pos=(0,0,0) rot=(1,0,0;3.14159rad)
  LinkPlacement = pos=(-45,-50,-28.65) rot=(-0.57735,0.57735,-0.57735;4.18879rad)
  LinkedObject = -> <external bearing_linear_8mm_horiz.FCStd>#Body
  Placement = pos=(-45,-50,-28.65) rot=(-0.57735,0.57735,-0.57735;4.18879rad)
  SolverId = Placement::ExpressionEngine
  expr: Placement = Body003.Placement * angle_machined_2in_25_drive_side#Local_CS.Placement * AttachmentOffset * bearing_linear_8mm_horiz#Local_CS004.Placement ^ -1
FEATURE [App::Link] Body008  label="shaft_upper"
  AttachedBy = #Local_CS
  AttachedTo = Body005#Local_CS001
  AttachmentOffset = pos=(0,0,0) rot=(-0.707107,-0.707107,0;3.14159rad)
  LinkPlacement = pos=(40,-25,406.35) rot=(-0.707107,0.707107,0;3.14159rad)
  LinkedObject = -> <external shaft_8mm.FCStd>#Body
  Placement = pos=(40,-25,406.35) rot=(-0.707107,0.707107,0;3.14159rad)
  SolverId = Placement::ExpressionEngine
  expr: Placement = Body005.Placement * support_shaft_horiz_8mm#Local_CS001.Placement * AttachmentOffset * shaft_8mm#Local_CS.Placement ^ -1
FEATURE [App::Link] upper_shaft  label="shaft_lower"
  AttachedBy = #Local_CS
  AttachedTo = Body006#Local_CS005
  LinkPlacement = pos=(-40,-25,406.35) rot=(0,1,0;3.14159rad)
  LinkedObject = -> <external shaft_8mm.FCStd>#Body
  Placement = pos=(-40,-25,406.35) rot=(0,1,0;3.14159rad)
  SolverId = Placement::ExpressionEngine
  expr: Placement = Body006.Placement * support_shaft_horiz_8mm#Local_CS005.Placement * AttachmentOffset * shaft_8mm#Local_CS.Placement ^ -1
FEATURE [App::Link] Body009
  AttachedBy = #Local_CS005
  AttachedTo = Body008#Local_CS001
  AttachmentOffset = pos=(0,0,0) rot=(0.707107,0.707107,0;3.14159rad)
  LinkPlacement = pos=(40,-25,401.35) rot=(0,0,1;0rad)
  LinkedObject = -> <external support_shaft_horiz_8mm.FCStd>#Body
  Placement = pos=(40,-25,401.35) rot=(0,0,1;0rad)
  SolverId = Placement::ExpressionEngine
  expr: Placement = Body008.Placement * shaft_8mm#Local_CS001.Placement * AttachmentOffset * support_shaft_horiz_8mm#Local_CS005.Placement ^ -1
FEATURE [App::Link] Body010
  AttachedBy = #Local_CS005
  AttachedTo = upper_shaft#Local_CS001
  AttachmentOffset = pos=(0,0,0) rot=(0,1,0;3.14159rad)
  LinkPlacement = pos=(-40,-25,401.35) rot=(0,0,1;3.14159rad)
  LinkedObject = -> <external support_shaft_horiz_8mm.FCStd>#Body
  Placement = pos=(-40,-25,401.35) rot=(0,0,1;3.14159rad)
  SolverId = Placement::ExpressionEngine
  expr: Placement = upper_shaft.Placement * shaft_8mm#Local_CS001.Placement * AttachmentOffset * support_shaft_horiz_8mm#Local_CS005.Placement ^ -1
FEATURE [App::Link] Body011
  AttachedBy = #Local_CS019
  AttachedTo = Body009#Local_CS002
  AttachmentOffset = pos=(0,0,0) rot=(0,0,1;4.71239rad)
  LinkPlacement = pos=(-1.705e-13,-39,406.35) rot=(-0.707107,0,-0.707107;3.14159rad)
  LinkedObject = -> <external angle_machined_2in_25_drive_side.FCStd>#Body
  Placement = pos=(-1.705e-13,-39,406.35) rot=(-0.707107,0,-0.707107;3.14159rad)
  SolverId = Placement::ExpressionEngine
  expr: Placement = Body009.Placement * support_shaft_horiz_8mm#Local_CS002.Placement * AttachmentOffset * angle_machined_2in_25_drive_side#Local_CS019.Placement ^ -1
FEATURE [App::Link] bearing_horiz_8_3
  AttachedBy = #Local_CS003
  AttachedTo = Body011#Local_CS
  AttachmentOffset = pos=(0,0,0) rot=(0,1,0;3.14159rad)
  LinkPlacement = pos=(45,-50,441.35) rot=(-0.57735,0.57735,-0.57735;4.18879rad)
  LinkedObject = -> <external bearing_linear_8mm_horiz.FCStd>#Body
  Placement = pos=(45,-50,441.35) rot=(-0.57735,0.57735,-0.57735;4.18879rad)
  SolverId = Placement::ExpressionEngine
  expr: Placement = Body011.Placement * angle_machined_2in_25_drive_side#Local_CS.Placement * AttachmentOffset * bearing_linear_8mm_horiz#Local_CS003.Placement ^ -1
FEATURE [App::Link] Body012
  AttachedBy = #Local_CS001
  AttachedTo = Body011#Local_CS009
  AttachmentOffset = pos=(0,0,0) rot=(1,0,0;3.14159rad)
  LinkPlacement = pos=(-45,-50,441.35) rot=(0.57735,0.57735,-0.57735;2.0944rad)
  LinkedObject = -> <external bearing_linear_8mm_horiz.FCStd>#Body
  Placement = pos=(-45,-50,441.35) rot=(0.57735,0.57735,-0.57735;2.0944rad)
  SolverId = Placement::ExpressionEngine
  expr: Placement = Body011.Placement * angle_machined_2in_25_drive_side#Local_CS009.Placement * AttachmentOffset * bearing_linear_8mm_horiz#Local_CS001.Placement ^ -1
FEATURE [App::Link] bearing_axial_2
  AttachedBy = #Local_CS001
  AttachedTo = Body011#Local_CS007
  LinkPlacement = pos=(-1.413e-13,7.82e-14,412.7) rot=(0,0,-1;1.5708rad)
  LinkedObject = -> <external KFL08_bushing.FCStd>#Body
  Placement = pos=(-1.413e-13,7.82e-14,412.7) rot=(0,0,-1;1.5708rad)
  SolverId = Placement::ExpressionEngine
  expr: Placement = Body011.Placement * angle_machined_2in_25_drive_side#Local_CS007.Placement * AttachmentOffset * KFL08_bushing#Local_CS001.Placement ^ -1
FEATURE [App::Link] Body013  label="Body"
  AttachedBy = #Local_CS001
  AttachedTo = Body002#Local_CS001
  AttachmentOffset = pos=(0,0,7) rot=(0,0,1;0rad)
  LinkPlacement = pos=(0.015,0.35,424.5) rot=(0.707107,0.707107,0;3.14159rad)
  LinkedObject = -> <external rod_threaded_8mm.FCStd>#Body
  Placement = pos=(0.015,0.35,424.5) rot=(0.707107,0.707107,0;3.14159rad)
  SolverId = Placement::ExpressionEngine
  expr: Placement = Body002.Placement * coupling_8mm_5mm#Local_CS001.Placement * AttachmentOffset * rod_threaded_8mm#Local_CS001.Placement ^ -1
FEATURE [App::Link] nut_angle_body
  AttachedBy = #Local_CS
  AttachedTo = Body003#Local_CS025
  AttachmentOffset = pos=(0,0,0) rot=(0,-1,0;3.14159rad)
  LinkPlacement = pos=(-5,-39,-4.15) rot=(0,-1,0;1.5708rad)
  LinkedObject = -> <external nut_angle.FCStd>#Body
  Placement = pos=(-5,-39,-4.15) rot=(0,-1,0;1.5708rad)
  SolverId = Placement::ExpressionEngine
  expr: Placement = Body003.Placement * angle_machined_2in_25_drive_side#Local_CS025.Placement * AttachmentOffset * nut_angle#Local_CS.Placement ^ -1
FEATURE [App::Link] nut_lead_screw_motor_side
  AttachedBy = #Local_CS002
  AttachedTo = nut_angle_body#Local_CS001
  AttachmentOffset = pos=(0,0,0) rot=(0.707107,-0.707107,0;3.14159rad)
  LinkPlacement = pos=(-5,-55.5,-4.15) rot=(0.357407,0.862856,0.357407;1.71777rad)
  LinkedObject = -> <external nut_lead_screw_tr8x4.FCStd>#Body
  Placement = pos=(-5,-55.5,-4.15) rot=(0.357407,0.862856,0.357407;1.71777rad)
  SolverId = Placement::ExpressionEngine
  expr: Placement = nut_angle_body.Placement * nut_angle#Local_CS001.Placement * AttachmentOffset * nut_lead_screw_tr8x4#Local_CS002.Placement ^ -1
FEATURE [App::Part] Assembly
  AssemblyType = Part::Link
  Group = -> [LCS_Origin,Variables,Constraints,Configurations,Body,Body001,Body002,Body003,Body004,Body005,Body006,Body007,bearing_lin2,Body008,upper_shaft,Body009,Body010,Body011,bearing_horiz_8_3,Body012,bearing_axial_2,Body013,nut_angle_body,nut_lead_screw_motor_side]
  LabelDocUser = drive_side_x-axis
  LabelPartUser = Assembly
  Origin = -> Origin
  Type = Assembly
---- part extruder_head_gear.FCStd = doc fcstd_cd6f2640c2ff ----
FCSTD DOCUMENT  (FreeCAD 0.19R)
Label: extruder_head_gear
License: All rights reserved
LicenseURL: http://en.wikipedia.org/wiki/All_rights_reserved
objects: Sketcher::SketchObject×12, PartDesign::Pad×10, PartDesign::Plane×3, PartDesign::CoordinateSystem×2, PartDesign::Chamfer×1, PartDesign::Line×1, PartDesign::Revolution×1, PartDesign::LinearPattern×1, PartDesign::Pocket×1, PartDesign::Mirrored×1, PartDesign::Body×1
note: 47 computed .brp shape members not serialized (recipe doc carries the construction recipe); baked Part::Feature solids carry a one-line shape summary decoded from their .brp

FEATURE [Sketcher::SketchObject] Sketch
  FullyConstrained = true
  MapMode = 5
  Placement = pos=(0,0,0) rot=(1,0,0;1.5708rad)
  Support = -> [XZ_Plane]
  sketch-geometry (4):
    g0: LineSegment StartX=-23.5 StartY=21.5 StartZ=0 EndX=23.5 EndY=21.5 EndZ=0
    g1: LineSegment StartX=23.5 StartY=21.5 StartZ=0 EndX=23.5 EndY=-21.5 EndZ=0
    g2: LineSegment StartX=23.5 StartY=-21.5 StartZ=0 EndX=-23.5 EndY=-21.5 EndZ=0
    g3: LineSegment StartX=-23.5 StartY=-21.5 StartZ=0 EndX=-23.5 EndY=21.5 EndZ=0
  constraints (11):
    c: Coincident(g0,g1)
    c: Coincident(g1,g2)
    c: Coincident(g2,g3)
    c: Coincident(g3,g0)
    c: Horizontal(g0)
    c: Horizontal(g2)
    c: Vertical(g1)
    c: Vertical(g3)
    c: Symmetric(g0,g2,g-1)
    c: DistanceX(g0,g0) = 47
    c: DistanceY(g1,g1) = 43
FEATURE [PartDesign::Pad] Pad
  Direction = (1,1,1)
  Length = 29.3624
  Length2 = 100
  Midplane = true
  Placement = pos=(0,0,0) rot=(1,0,0;1.5708rad)
  Profile = -> Sketch
  Refine = true
  Type = 0
FEATURE [Sketcher::SketchObject] Sketch001
  FullyConstrained = true
  MapMode = 5
  Placement = pos=(0,0,0) rot=(1,0,0;1.5708rad)
  Support = -> [XZ_Plane]
  sketch-geometry (1):
    g0: Circle CenterX=15 CenterY=15 CenterZ=0 NormalX=0 NormalY=0 NormalZ=1 AngleXU=0 Radius=17.0434
  constraints (3):
    c: Diameter(g0) = 34.0868
    c: DistanceX(g-1,g0) = 15
    c: DistanceY(g-1,g0) = 15
FEATURE [PartDesign::Pad] Pad001
  BaseFeature = -> Pad
  Direction = (1,1,1)
  Length = 8
  Length2 = -20
  Placement = pos=(0,0,0) rot=(1,0,0;1.5708rad)
  Profile = -> Sketch001
  Refine = true
  Reversed = true
  Type = 0
FEATURE [Sketcher::SketchObject] Sketch002
  ExternalGeometry = -> [Pad001]
  FullyConstrained = true
  MapMode = 5
  Support = -> [XY_Plane]
  expr: Constraints[14] = 0.54in
  sketch-geometry (5):
    g0: LineSegment StartX=11 StartY=4.9652 StartZ=0 EndX=19 EndY=4.9652 EndZ=0
    g1: LineSegment StartX=19 StartY=4.9652 StartZ=0 EndX=19 EndY=-3.0348 EndZ=0
    g2: LineSegment StartX=19 StartY=-3.0348 StartZ=0 EndX=11 EndY=-3.0348 EndZ=0
    g3: LineSegment StartX=11 StartY=-3.0348 StartZ=0 EndX=11 EndY=4.9652 EndZ=0
    g4: Circle CenterX=15 CenterY=0.9652 CenterZ=0 NormalX=0 NormalY=0 NormalZ=1 AngleXU=0 Radius=4
  constraints (15):
    c: Coincident(g0,g1)
    c: Coincident(g1,g2)
    c: Coincident(g2,g3)
    c: Coincident(g3,g0)
    c: Horizontal(g0)
    c: Horizontal(g2)
    c: Vertical(g1)
    c: Vertical(g3)
    c: Equal(g1,g0)
    c: DistanceY(g1,g1) = 8
    c: Tangent(g4,g0)
    c: Tangent(g4,g3)
    c: Tangent(g4,g1)
    c: DistanceX(g-1,g4) = 15
    c: DistanceY(g4,g-3) = 13.716
FEATURE [PartDesign::Pad] Pad002
  BaseFeature = -> Pad001
  Direction = (1,1,1)
  Length = 35
  Length2 = 100
  Placement = pos=(0,0,0) rot=(1,0,0;1.5708rad)
  Profile = -> Sketch002
  Refine = true
  Type = 0
FEATURE [Sketcher::SketchObject] Sketch003
  ExternalGeometry = -> [Pad002]
  FullyConstrained = true
  MapMode = 5
  Placement = pos=(0,0,35) rot=(0,0,1;3.14159rad)
  Support = -> [Pad002]
  expr: Constraints[4] = 4
  sketch-geometry (2):
    g0: Circle CenterX=-15 CenterY=-0.9652 CenterZ=0 NormalX=0 NormalY=0 NormalZ=1 AngleXU=0 Radius=4
    g1: Circle CenterX=-15 CenterY=-0.9652 CenterZ=0 NormalX=0 NormalY=0 NormalZ=1 AngleXU=0 Radius=2
  constraints (5):
    c: Tangent(g0,g-5)
    c: Tangent(g0,g-3)
    c: Tangent(g0,g-4)
    c: Coincident(g1,g0)
    c: Diameter(g1) = 4
FEATURE [PartDesign::Pad] Pad003
  BaseFeature = -> Pad002
  Direction = (1,1,1)
  Length = 2
  Length2 = 100
  Placement = pos=(0,0,0) rot=(1,0,0;1.5708rad)
  Profile = -> Sketch003
  Refine = true
  Type = 0
FEATURE [Sketcher::SketchObject] Sketch004
  ExternalGeometry = -> [Pad003]
  FullyConstrained = true
  MapMode = 5
  Placement = pos=(-23.5,0,0) rot=(0.707107,0,-0.707107;3.14159rad)
  Support = -> [Pad003]
  sketch-geometry (1):
    g0: Circle CenterX=-21.5 CenterY=2.6812 CenterZ=0 NormalX=0 NormalY=0 NormalZ=1 AngleXU=0 Radius=7
  constraints (3):
    c: Diameter(g0) = 14
    c: DistanceY(g0,g-3) = 12
    c: Vertical(g-3,g0)
FEATURE [PartDesign::Pad] Pad004
  BaseFeature = -> Pad003
  Direction = (1,1,1)
  Length = 6.858
  Length2 = 100
  Placement = pos=(0,0,0) rot=(1,0,0;1.5708rad)
  Profile = -> Sketch004
  Refine = true
  Type = 0
  expr: Length = 0.27in
FEATURE [Sketcher::SketchObject] Sketch005
  ExternalGeometry = -> [Pad004]
  FullyConstrained = true
  MapMode = 5
  Placement = pos=(0,0,0) rot=(1,0,0;1.5708rad)
  Support = -> [XZ_Plane]
  sketch-geometry (6):
    g0: ArcOfCircle CenterX=13.6649 CenterY=38.5038 CenterZ=0 NormalX=0 NormalY=0 NormalZ=1 AngleXU=0 Radius=16.1649 StartAngle=2.51996 EndAngle=3.91947
    g1: ArcOfCircle CenterX=13.6649 CenterY=38.5038 CenterZ=0 NormalX=0 NormalY=0 NormalZ=1 AngleXU=0 Radius=17.1649 StartAngle=2.51996 EndAngle=3.14159
    g2: LineSegment StartX=-3.5 StartY=38.5038 StartZ=0 EndX=-3.5 EndY=21.5 EndZ=0
    g3: LineSegment StartX=-0.288926 StartY=48.5 StartZ=0 EndX=0.524002 EndY=47.9176 EndZ=0
    g4: LineSegment StartX=-3.5 StartY=21.5 StartZ=0 EndX=2.1489 EndY=21.5 EndZ=0
    g5: LineSegment StartX=2.1489 StartY=27.1598 StartZ=0 EndX=2.1489 EndY=21.5 EndZ=0
  constraints (19):
    c: Coincident(g1,g0)
    c: Coincident(g2,g1)
    c: Tangent(g1,g2)
    c: Vertical(g2)
    c: Coincident(g3,g1)
    c: Coincident(g3,g0)
    c: Coincident(g4,g2)
    c: Distance(g3) = 1
    c: PointOnObject(g0,g3)
    c: Horizontal(g4)
    c: DistanceX(g-3,g2) = 20
    c: DistanceY(g-3,g1) = 27
    c: Vertical(g5)
    c: Coincident(g0,g5)
    c: Coincident(g4,g5)
    c: DistanceX(g4,g4) = 5.6489
    c: Radius(g0) = 16.1649
    c: DistanceY(g5,g5) = 5.6598
    c: Horizontal(g4,g-3)
FEATURE [PartDesign::Pad] Pad005
  BaseFeature = -> Pad004
  Direction = (1,1,1)
  Length = 5
  Length2 = 7
  Placement = pos=(0,0,0) rot=(1,0,0;1.5708rad)
  Profile = -> Sketch005
  Refine = true
  Type = 4
FEATURE [Sketcher::SketchObject] Sketch006
  ExternalGeometry = -> [Pad005]
  FullyConstrained = true
  MapMode = 5
  Support = -> [XY_Plane]
  sketch-geometry (1):
    g0: Circle CenterX=15 CenterY=0.9652 CenterZ=0 NormalX=0 NormalY=0 NormalZ=1 AngleXU=0 Radius=3.5433
  constraints (2):
    c: Coincident(g-3,g0)
    c: Diameter(g0) = 7.0866
FEATURE [PartDesign::Pad] Pad006
  BaseFeature = -> Pad005
  Direction = (1,1,1)
  Length = 70
  Length2 = 100
  Placement = pos=(0,0,0) rot=(1,0,0;1.5708rad)
  Profile = -> Sketch006
  Refine = true
  Reversed = true
  Type = 0
FEATURE [PartDesign::Chamfer] Chamfer
  Angle = 45
  Base = -> Pad006 [Edge80]
  BaseFeature = -> Pad006
  ChamferType = 0
  FlipDirection = false
  Placement = pos=(0,0,0) rot=(1,0,0;1.5708rad)
  Refine = true
  Size = 3.4
  Size2 = 1
  SupportTransform = false
FEATURE [PartDesign::Line] DatumLine
  AttacherType = Attacher::AttachEngineLine
  Length = 20
  MapMode = 19
  Placement = pos=(15,0.9652,-66.6) rot=(0,0,1;0rad)
  ResizeMode = 0
  Support = -> [Chamfer]
FEATURE [PartDesign::Plane] DatumPlane
  Length = 63.5351
  MapMode = 3
  Placement = pos=(15,0.9652,-66.6) rot=(1,0,0;1.5708rad)
  ResizeMode = 0
  Support = -> [DatumLine]
  Width = 105.135
FEATURE [Sketcher::SketchObject] Sketch007
  ExternalGeometry = -> [Chamfer]
  FullyConstrained = true
  MapMode = 5
  Placement = pos=(15,0.9652,-66.6) rot=(1,0,0;1.5708rad)
  Support = -> [DatumPlane]
  expr: Constraints[9] = 22.5 / 2
  sketch-geometry (4):
    g0: LineSegment StartX=0 StartY=41.1 StartZ=0 EndX=11.25 EndY=41.1 EndZ=0
    g1: LineSegment StartX=11.25 StartY=41.1 StartZ=0 EndX=11.25 EndY=40.1 EndZ=0
    g2: LineSegment StartX=11.25 StartY=40.1 StartZ=0 EndX=0 EndY=40.1 EndZ=0
    g3: LineSegment StartX=0 StartY=40.1 StartZ=0 EndX=0 EndY=41.1 EndZ=0
  constraints (12):
    c: Coincident(g0,g1)
    c: Coincident(g1,g2)
    c: Coincident(g2,g3)
    c: Coincident(g3,g0)
    c: Horizontal(g0)
    c: Horizontal(g2)
    c: Vertical(g1)
    c: Vertical(g3)
    c: Vertical(g-1,g2)
    c: DistanceX(g-1,g1) = 11.25
    c: DistanceY(g1,g1) = 1
    c: DistanceY(g0,g-3) = 4
FEATURE [PartDesign::Revolution] Revolution
  Angle = 360
  Axis = (0,2e-16,1)
  Base = (15,0.9652,-66.6)
  BaseFeature = -> Chamfer
  Placement = pos=(0,0,0) rot=(1,0,0;1.5708rad)
  Profile = -> Sketch007
  ReferenceAxis = -> Sketch007 [V_Axis]
  Refine = true
  Reversed = true
FEATURE [PartDesign::LinearPattern] LinearPattern
  BaseFeature = -> Revolution
  Direction = -> Z_Axis
  Length = 25
  Occurrences = 11
  Originals = -> [Revolution]
  Placement = pos=(0,0,0) rot=(1,0,0;1.5708rad)
  Refine = true
  Reversed = true
FEATURE [PartDesign::Plane] DatumPlane001
  AttachmentOffset = pos=(0,0,-53) rot=(0,0,1;0rad)
  Length = 60
  MapMode = 5
  Placement = pos=(0,0,-53) rot=(0,0,1;0rad)
  ResizeMode = 0
  Support = -> [XY_Plane]
  Width = 60
FEATURE [Sketcher::SketchObject] Sketch008
  ExternalGeometry = -> [LinearPattern]
  FullyConstrained = true
  MapMode = 5
  Placement = pos=(0,0,-53) rot=(0,0,1;0rad)
  Support = -> [DatumPlane001]
  sketch-geometry (4):
    g0: LineSegment StartX=-1 StartY=-6.5348 StartZ=0 EndX=19 EndY=-6.5348 EndZ=0
    g1: LineSegment StartX=19 StartY=-6.5348 StartZ=0 EndX=19 EndY=8.4652 EndZ=0
    g2: LineSegment StartX=19 StartY=8.4652 StartZ=0 EndX=-1 EndY=8.4652 EndZ=0
    g3: LineSegment StartX=-1 StartY=8.4652 StartZ=0 EndX=-1 EndY=-6.5348 EndZ=0
  constraints (12):
    c: Coincident(g0,g1)
    c: Coincident(g1,g2)
    c: Coincident(g2,g3)
    c: Coincident(g3,g0)
    c: Horizontal(g0)
    c: Horizontal(g2)
    c: Vertical(g1)
    c: Vertical(g3)
    c: DistanceX(g0,g0) = 20
    c: DistanceY(g1,g1) = 15
    c: DistanceY(g-3,g1) = 7.5
    c: DistanceX(g-3,g0) = 4
FEATURE [PartDesign::Pad] Pad007
  BaseFeature = -> LinearPattern
  Direction = (1,1,1)
  Length = 12
  Length2 = 100
  Placement = pos=(0,0,0) rot=(1,0,0;1.5708rad)
  Profile = -> Sketch008
  Refine = true
  Reversed = true
  Type = 0
FEATURE [Sketcher::SketchObject] Sketch009
  ExternalGeometry = -> [Pad007]
  FullyConstrained = true
  MapMode = 5
  Placement = pos=(0,0,-65) rot=(1,0,0;3.14159rad)
  Support = -> [Pad007]
  sketch-geometry (7):
    g0: LineSegment StartX=18.5433 StartY=1.08053 StartZ=0 EndX=15 EndY=3.12625 EndZ=0
    g1: LineSegment StartX=15 StartY=3.12625 StartZ=0 EndX=11.4567 EndY=1.08053 EndZ=0
    g2: LineSegment StartX=11.4567 StartY=1.08053 StartZ=0 EndX=11.4567 EndY=-3.01093 EndZ=0
    g3: LineSegment StartX=11.4567 StartY=-3.01093 StartZ=0 EndX=15 EndY=-5.05665 EndZ=0
    g4: LineSegment StartX=15 StartY=-5.05665 StartZ=0 EndX=18.5433 EndY=-3.01093 EndZ=0
    g5: LineSegment StartX=18.5433 StartY=-3.01093 StartZ=0 EndX=18.5433 EndY=1.08053 EndZ=0
    g6: Circle CenterX=15 CenterY=-0.9652 CenterZ=0 NormalX=0 NormalY=0 NormalZ=1 AngleXU=0 Radius=4.09145
  constraints (16):
    c: Coincident(g0,g1)
    c: Coincident(g1,g2)
    c: Coincident(g2,g3)
    c: Coincident(g3,g4)
    c: Coincident(g4,g5)
    c: Coincident(g5,g0)
    c: Equal(g0, g1-g5) x5
    c: PointOnObject(g0,g6)
    c: PointOnObject(g1,g6)
    c: PointOnObject(g2,g6)
    c: PointOnObject(g3,g6)
    c: PointOnObject(g4,g6)
    c: PointOnObject(g5,g6)
    c: Vertical(g5)
    c: Coincident(g6,g-3)
    c: Tangent(g-3,g2)
FEATURE [PartDesign::Pad] Pad008
  BaseFeature = -> Pad007
  Direction = (1,1,1)
  Length = 2.5
  Length2 = 100
  Placement = pos=(0,0,0) rot=(1,0,0;1.5708rad)
  Profile = -> Sketch009
  Refine = true
  Type = 0
FEATURE [Sketcher::SketchObject] Sketch010
  FullyConstrained = true
  MapMode = 5
  Placement = pos=(0,0,0) rot=(1,0,0;1.5708rad)
  Support = -> [XZ_Plane]
  sketch-geometry (1):
    g0: Circle CenterX=0 CenterY=0 CenterZ=0 NormalX=0 NormalY=0 NormalZ=1 AngleXU=0 Radius=1
  constraints (2):
    c: Diameter(g0) = 2
    c: Coincident(g0,g-1)
FEATURE [PartDesign::Pocket] Pocket
  BaseFeature = -> Pad008
  Length = 5
  Length2 = 100
  Placement = pos=(0,0,0) rot=(1,0,0;1.5708rad)
  Profile = -> Sketch010
  Refine = true
  Type = 1
FEATURE [PartDesign::Plane] DatumPlane002
  AttachmentOffset = pos=(0,0,-24) rot=(0,0,1;0rad)
  Length = 60
  MapMode = 2
  Placement = pos=(0,0,-24) rot=(0,0,1;0rad)
  ResizeMode = 0
  Support = -> [XY_Plane]
  Width = 60
FEATURE [Sketcher::SketchObject] Sketch011
  ExternalGeometry = -> [Pocket]
  FullyConstrained = true
  MapMode = 5
  Placement = pos=(0,0,-24) rot=(0,0,1;0rad)
  Support = -> [DatumPlane002]
  sketch-geometry (7):
    g0: ArcOfCircle CenterX=15 CenterY=0.9652 CenterZ=0 NormalX=0 NormalY=0 NormalZ=1 AngleXU=0 Radius=10.75 StartAngle=0 EndAngle=2.19655
    g1: LineSegment StartX=8.70366 StartY=9.67833 StartZ=0 EndX=8.11795 EndY=10.4888 EndZ=0
    g2: ArcOfCircle CenterX=15 CenterY=0.9652 CenterZ=0 NormalX=0 NormalY=0 NormalZ=1 AngleXU=0 Radius=11.75 StartAngle=1.76298 EndAngle=2.19655
    g3: LineSegment StartX=25.75 StartY=0.9652 StartZ=0 EndX=40 EndY=0.9652 EndZ=0
    g4: LineSegment StartX=12.7557 StartY=12.4989 StartZ=0 EndX=28 EndY=15.4652 EndZ=0
    g5: LineSegment StartX=28 StartY=15.4652 StartZ=0 EndX=40 EndY=15.4652 EndZ=0
    g6: LineSegment StartX=40 StartY=15.4652 StartZ=0 EndX=40 EndY=0.9652 EndZ=0
  constraints (20):
    c: Coincident(g-3,g0)
    c: Radius(g0) = 10.75
    c: Coincident(g1,g0)
    c: PointOnObject(g0,g1)
    c: Coincident(g2,g0)
    c: Coincident(g2,g1)
    c: Distance(g1) = 1
    c: Coincident(g0,g3)
    c: PointOnObject(g0,g3)
    c: Horizontal(g3)
    c: Angle(g3,g1) = 2.19655
    c: Coincident(g5,g4)
    c: Horizontal(g5)
    c: Coincident(g6,g5)
    c: Vertical(g6)
    c: Tangent(g2,g4) = 1.5708
    c: Coincident(g6,g3)
    c: DistanceX(g0,g3) = 25
    c: DistanceX(g0,g4) = 13
    c: DistanceY(g6,g6) = 14.5
FEATURE [PartDesign::Pad] Pad009
  BaseFeature = -> Pocket
  Direction = (1,1,1)
  Length = 29
  Length2 = 100
  Placement = pos=(0,0,0) rot=(1,0,0;1.5708rad)
  Profile = -> Sketch011
  Refine = true
  Reversed = true
  Type = 0
FEATURE [PartDesign::Mirrored] Mirrored  label="Extruder"
  BaseFeature = -> Pad009
  MirrorPlane = -> DatumPlane
  Originals = -> [Pad009]
  Placement = pos=(0,0,0) rot=(1,0,0;1.5708rad)
FEATURE [PartDesign::CoordinateSystem] Local_CS001  label="Local_tip"
  AttacherType = Attacher::AttachEngine3D
  AttachmentOffset = pos=(0,0,0) rot=(0,0,-1;1.5708rad)
  MapMode = 11
  Placement = pos=(15,0.9652,-70) rot=(0,0,1;0rad)
  Support = -> [Mirrored]
FEATURE [PartDesign::CoordinateSystem] Local_CS  label="motor_bracket"
  AttacherType = Attacher::AttachEngine3D
  MapMode = 11
  Placement = pos=(0,14.6812,4.9e-15) rot=(0.57735,-0.57735,0.57735;2.0944rad)
  Support = -> [Mirrored]
FEATURE [PartDesign::Body] Body
  Group = -> [Sketch,Pad,Sketch001,Pad001,Sketch002,Pad002,Sketch003,Pad003,Sketch004,Pad004,Sketch005,Pad005,Sketch006,Pad006,Chamfer,DatumLine,DatumPlane,Sketch007,Revolution,LinearPattern,DatumPlane001,Sketch008,Pad007,Sketch009,Pad008,Sketch010,Pocket,DatumPlane002,Sketch011,Pad009,Mirrored,Local_CS001,Local_CS]
  Origin = -> Origin
  Tip = -> Mirrored
---- part nut_lead_screw_tr8x4.FCStd = doc fcstd_da8f933943eb ----
FCSTD DOCUMENT  (FreeCAD 0.19R)
Label: nut_lead_screw_tr8x4
License: All rights reserved
LicenseURL: http://en.wikipedia.org/wiki/All_rights_reserved
objects: Sketcher::SketchObject×3, PartDesign::CoordinateSystem×3, PartDesign::Revolution×1, PartDesign::Pocket×1, PartDesign::Hole×1, PartDesign::PolarPattern×1, PartDesign::Body×1
note: 14 computed .brp shape members not serialized (recipe doc carries the construction recipe); baked Part::Feature solids carry a one-line shape summary decoded from their .brp

FEATURE [Sketcher::SketchObject] Sketch
  FullyConstrained = true
  MapMode = 5
  Placement = pos=(0,0,0) rot=(0.57735,0.57735,0.57735;2.0944rad)
  Support = -> [YZ_Plane]
  sketch-geometry (8):
    g0: LineSegment StartX=0 StartY=0 StartZ=0 EndX=11 EndY=0 EndZ=0
    g1: LineSegment StartX=11 StartY=0 StartZ=0 EndX=11 EndY=-4 EndZ=0
    g2: LineSegment StartX=11 StartY=-4 StartZ=0 EndX=5.15 EndY=-4 EndZ=0
    g3: LineSegment StartX=5.15 StartY=-4 StartZ=0 EndX=5.15 EndY=-22 EndZ=0
    g4: LineSegment StartX=7 StartY=-26 StartZ=0 EndX=0 EndY=-26 EndZ=0
    g5: LineSegment StartX=0 StartY=-26 StartZ=0 EndX=0 EndY=0 EndZ=0
    g6: LineSegment StartX=5.15 StartY=-22 StartZ=0 EndX=7 EndY=-22 EndZ=0
    g7: LineSegment StartX=7 StartY=-22 StartZ=0 EndX=7 EndY=-26 EndZ=0
  constraints (23):
    c: Horizontal(g0)
    c: Vertical(g1)
    c: Coincident(g1,g2)
    c: Horizontal(g2)
    c: Coincident(g2,g3)
    c: Vertical(g3)
    c: PointOnObject(g4,g-2)
    c: Horizontal(g4)
    c: Coincident(g4,g5)
    c: Coincident(g5,g0)
    c: Horizontal(g6)
    c: Coincident(g7,g6)
    c: Vertical(g7)
    c: Coincident(g3,g6)
    c: Coincident(g4,g7)
    c: DistanceX(g-1,g4) = 7
    c: Coincident(g1,g0)
    c: Coincident(g-1,g0)
    c: DistanceX(g0,g0) = 11
    c: DistanceX(g0,g2) = 5.15
    c: DistanceY(g1,g1) = 4
    c: DistanceY(g5,g5) = 26
    c: DistanceY(g7,g7) = 4
FEATURE [PartDesign::Revolution] Revolution
  Angle = 360
  Axis = (-2e-16,3e-16,1)
  Base = (0,0,0)
  Placement = pos=(0,0,0) rot=(0.57735,0.57735,0.57735;2.0944rad)
  Profile = -> Sketch
  ReferenceAxis = -> Sketch [V_Axis]
  Reversed = true
FEATURE [Sketcher::SketchObject] Sketch001
  FullyConstrained = true
  MapMode = 5
  Support = -> [XY_Plane]
  sketch-geometry (1):
    g0: Circle CenterX=0 CenterY=0 CenterZ=0 NormalX=0 NormalY=0 NormalZ=1 AngleXU=0 Radius=4
  constraints (2):
    c: Coincident(g0,g-1)
    c: Diameter(g0) = 8
FEATURE [PartDesign::Pocket] Pocket
  BaseFeature = -> Revolution
  Length = 5
  Length2 = 100
  Midplane = true
  Placement = pos=(0,0,0) rot=(0.57735,0.57735,0.57735;2.0944rad)
  Profile = -> Sketch001
  Type = 1
FEATURE [Sketcher::SketchObject] Sketch002
  FullyConstrained = true
  MapMode = 5
  Support = -> [XY_Plane]
  sketch-geometry (1):
    g0: Circle CenterX=0 CenterY=8 CenterZ=0 NormalX=0 NormalY=0 NormalZ=1 AngleXU=0 Radius=1.5
  constraints (3):
    c: Diameter(g0) = 3
    c: Vertical(g0,g-1)
    c: DistanceY(g-1,g0) = 8
FEATURE [PartDesign::Hole] Hole
  BaseFeature = -> Pocket
  Depth = 10
  DepthType = 0
  Diameter = 3.4
  DrillForDepth = false
  DrillPoint = 1
  DrillPointAngle = 118
  HoleCutCountersinkAngle = 90
  HoleCutCustomValues = false
  HoleCutDepth = 3.4
  HoleCutDiameter = 6.1
  HoleCutType = 0
  ModelActualThread = false
  Placement = pos=(0,0,0) rot=(0.57735,0.57735,0.57735;2.0944rad)
  Profile = -> Sketch002
  Tapered = false
  TaperedAngle = 90
  ThreadAngle = 60
  ThreadClass = 0
  ThreadCutOffInner = 0.0541266
  ThreadCutOffOuter = 0.108253
  ThreadDirection = 0
  ThreadFit = 0
  ThreadPitch = 0.5
  ThreadSize = 9
  ThreadType = 1
  Threaded = false
FEATURE [PartDesign::PolarPattern] PolarPattern
  Angle = 360
  Axis = -> Sketch002 [N_Axis]
  BaseFeature = -> Hole
  Occurrences = 4
  Originals = -> [Hole]
  Placement = pos=(0,0,0) rot=(0.57735,0.57735,0.57735;2.0944rad)
FEATURE [PartDesign::CoordinateSystem] Local_CS  label="lcs_screw1"
  AttacherType = Attacher::AttachEngine3D
  AttachmentOffset = pos=(0,0,0) rot=(0,0,1;3.14159rad)
  MapMode = 11
  Placement = pos=(-8,0,-2e-15) rot=(0.707107,-0.707107,0;3.14159rad)
  Support = -> [PolarPattern]
FEATURE [PartDesign::CoordinateSystem] Local_CS001  label="lcs_nut_lead_screw"
  AttacherType = Attacher::AttachEngine3D
  AttachmentOffset = pos=(0,0,0) rot=(0,0,1;0.785398rad)
  MapMode = 11
  Placement = pos=(1.8e-15,-9e-16,-4) rot=(0.92388,-0.382683,0;3.14159rad)
  Support = -> [PolarPattern]
FEATURE [PartDesign::CoordinateSystem] Local_CS002
  AttacherType = Attacher::AttachEngine3D
  AttachmentOffset = pos=(0,0,0) rot=(0,0,1;0.785398rad)
  MapMode = 11
  Placement = pos=(-8.9e-15,-9.1e-15,0) rot=(0,0,1;2.35619rad)
  Support = -> [PolarPattern]
FEATURE [PartDesign::Body] Body
  Group = -> [Sketch,Revolution,Sketch001,Pocket,Sketch002,Hole,PolarPattern,Local_CS,Local_CS001,Local_CS002]
  Origin = -> Origin
  Tip = -> PolarPattern
---- part screw_shc_M3x12.FCStd = doc fcstd_817e04169b75 ----
FCSTD DOCUMENT  (FreeCAD 0.19R)
Label: screw_shc_M3x12
License: All rights reserved
LicenseURL: http://en.wikipedia.org/wiki/All_rights_reserved
objects: Part::Feature×1, PartDesign::CoordinateSystem×1, Sketcher::SketchObject×1, PartDesign::Pad×1, PartDesign::Body×1
note: 6 computed .brp shape members not serialized (recipe doc carries the construction recipe); baked Part::Feature solids carry a one-line shape summary decoded from their .brp

FEATURE [Part::Feature] _1292A114_18_8_Stainless_Steel_Socket_Head_Screw  label="screw_shc_M3x12"
  shape: bbox 5.5 x 5.5 x 15.03 mm, 125 faces, 0 solids (baked)
FEATURE [PartDesign::CoordinateSystem] Local_CS  label="LCS_screw_shc_M3x12"
  AttacherType = Attacher::AttachEngine3D
  MapMode = 11
  Placement = pos=(0,0,-12) rot=(-0.707107,0.707107,0;3.14159rad)
FEATURE [Sketcher::SketchObject] Sketch
  FullyConstrained = true
  MapMode = 5
  Support = -> [XY_Plane]
  sketch-geometry (1):
    g0: Circle CenterX=0 CenterY=0 CenterZ=0 NormalX=0 NormalY=0 NormalZ=1 AngleXU=0 Radius=1.25
  constraints (2):
    c: Coincident(g0,g-1)
    c: Diameter(g0) = 2.5
FEATURE [PartDesign::Pad] Pad
  Direction = (1,1,1)
  Length = 3
  Length2 = 100
  Profile = -> Sketch
  Refine = true
  Type = 0
FEATURE [PartDesign::Body] Body
  Group = -> [Local_CS,Sketch,Pad]
  Origin = -> Origin
  Tip = -> Pad
---- part screw_shc_M3x16.FCStd = doc fcstd_d9eea96b572a ----
FCSTD DOCUMENT  (FreeCAD 0.19R)
Label: screw_shc_M3x16
License: All rights reserved
LicenseURL: http://en.wikipedia.org/wiki/All_rights_reserved
objects: Part::Feature×1, PartDesign::ShapeBinder×1, PartDesign::CoordinateSystem×1, PartDesign::FeatureBase×1, PartDesign::Body×1
note: 5 computed .brp shape members not serialized (recipe doc carries the construction recipe); baked Part::Feature solids carry a one-line shape summary decoded from their .brp

FEATURE [Part::Feature] _1292A115_18_8_Stainless_Steel_Socket_Head_Screw
  shape: bbox 5.5 x 5.5 x 19.03 mm, 157 faces, 0 solids (baked)
FEATURE [PartDesign::ShapeBinder] Copy_1292A115_18_8_Stainless_Steel_Socket_Head_Screw
  TraceSupport = false
FEATURE [PartDesign::CoordinateSystem] Local_CS
  AttacherType = Attacher::AttachEngine3D
  MapMode = 11
  Placement = pos=(0,0,-16) rot=(-0.707107,0.707107,0;3.14159rad)
  Support = -> [Copy_1292A115_18_8_Stainless_Steel_Socket_Head_Screw]
FEATURE [PartDesign::FeatureBase] BaseFeature
  BaseFeature = -> _1292A115_18_8_Stainless_Steel_Socket_Head_Screw
FEATURE [PartDesign::Body] Body
  BaseFeature = -> _1292A115_18_8_Stainless_Steel_Socket_Head_Screw
  Group = -> [BaseFeature,Local_CS,Copy_1292A115_18_8_Stainless_Steel_Socket_Head_Screw]
  Origin = -> Origin
  Tip = -> BaseFeature
---- part washer_M5.FCStd = doc fcstd_f6e5a775d055 ----
FCSTD DOCUMENT  (FreeCAD 0.19R)
Label: washer_M5
License: All rights reserved
LicenseURL: http://en.wikipedia.org/wiki/All_rights_reserved
objects: PartDesign::CoordinateSystem×2, Sketcher::SketchObject×1, PartDesign::Pad×1, PartDesign::Body×1
note: 6 computed .brp shape members not serialized (recipe doc carries the construction recipe); baked Part::Feature solids carry a one-line shape summary decoded from their .brp

FEATURE [Sketcher::SketchObject] Sketch
  FullyConstrained = true
  MapMode = 5
  Placement = pos=(0,0,0) rot=(1,0,0;1.5708rad)
  Support = -> [XZ_Plane]
  sketch-geometry (2):
    g0: Circle CenterX=0 CenterY=0 CenterZ=0 NormalX=0 NormalY=0 NormalZ=1 AngleXU=0 Radius=3
    g1: Circle CenterX=0 CenterY=0 CenterZ=0 NormalX=0 NormalY=0 NormalZ=1 AngleXU=0 Radius=1.6
  constraints (4):
    c: Coincident(g0,g-1)
    c: Coincident(g1,g0)
    c: Diameter(g1) = 3.2
    c: Diameter(g0) = 6
FEATURE [PartDesign::Pad] Pad
  Direction = (1,1,1)
  Length = 0.5
  Length2 = 100
  Midplane = true
  Placement = pos=(0,0,0) rot=(1,0,0;1.5708rad)
  Profile = -> Sketch
  Refine = true
  Type = 0
FEATURE [PartDesign::CoordinateSystem] Local_CS  label="Local_washer_side1"
  AttacherType = Attacher::AttachEngine3D
  MapMode = 11
  Placement = pos=(0,-0.25,0) rot=(0.57735,-0.57735,0.57735;2.0944rad)
  Support = -> [Pad]
FEATURE [PartDesign::CoordinateSystem] Local_CS001  label="Local_washer_side2"
  AttacherType = Attacher::AttachEngine3D
  MapMode = 11
  Placement = pos=(0,0.25,0) rot=(0.57735,-0.57735,0.57735;2.0944rad)
  Support = -> [Pad]
FEATURE [PartDesign::Body] Body
  Group = -> [Sketch,Pad,Local_CS,Local_CS001]
  Origin = -> Origin
  Tip = -> Pad
